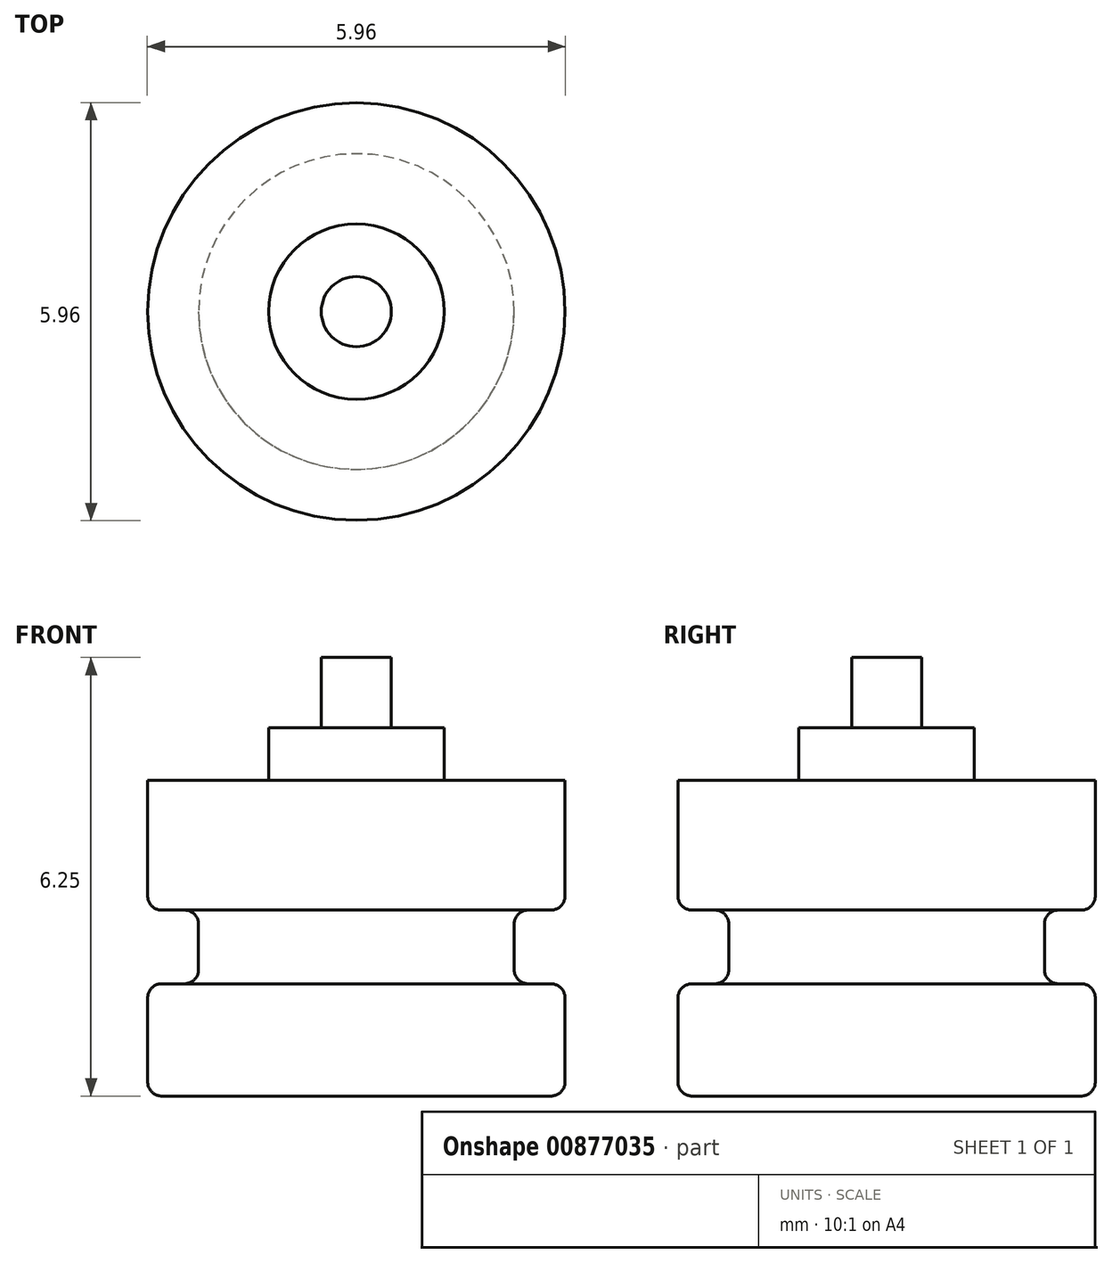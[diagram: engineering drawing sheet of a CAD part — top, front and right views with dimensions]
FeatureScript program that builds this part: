
annotation { "Feature Type Name" : "Feature", "Feature Type Description" : "" }
export const myFeature = defineFeature(function(context is Context, id is Id, definition is map)
    precondition{}
    {
        {
            var Q0;
            Q0=qCreatedBy(makeId("Front.planeOp"),FACE);
            var sketch = newSketch(context, id + "F0", { "sketchPlane" : qUnion([Q0])});
            skLineSegment(sketch, "E0", {"start": v(0, 0) * mm, "end": v(-2.97, 0) * mm});
            skLineSegment(sketch, "E1", {"start": v(-2.98, 0) * mm, "end": v(-2.98, 1.6) * mm});
            skLineSegment(sketch, "E2", {"start": v(-2.97, 1.6) * mm, "end": v(-2.25, 1.6) * mm});
            skLineSegment(sketch, "E3", {"start": v(-2.25, 1.6) * mm, "end": v(-2.25, 2.65) * mm});
            skLineSegment(sketch, "E4", {"start": v(-2.25, 2.65) * mm, "end": v(-2.98, 2.65) * mm});
            skLineSegment(sketch, "E5", {"start": v(-2.98, 2.65) * mm, "end": v(-2.98, 4.5) * mm});
            skLineSegment(sketch, "E6", {"start": v(-2.98, 4.5) * mm, "end": v(-1.25, 4.5) * mm});
            skLineSegment(sketch, "E7", {"start": v(-1.25, 4.5) * mm, "end": v(-1.25, 5.25) * mm});
            skLineSegment(sketch, "E8", {"start": v(-1.25, 5.25) * mm, "end": v(-0.5, 5.25) * mm});
            skLineSegment(sketch, "E9", {"start": v(-0.5, 5.25) * mm, "end": v(-0.5, 6.25) * mm});
            skLineSegment(sketch, "E10", {"start": v(-0.5, 6.25) * mm, "end": v(0, 6.25) * mm});
            skLineSegment(sketch, "E11", {"start": v(0, 6.25) * mm, "end": v(0, 0) * mm});
            skSolve(sketch);
        }
        {
            var Q0;
            Q0=makeQuery(id+"F0.imprint","IMPRINT",FACE,{"disambiguationData":[TD([[makeQuery(id+"F0.imprint","IMPRINT",EDGE,{"derivedFrom":sQuery(id+"F0.wireOp",EDGE,"E0")}),-1.0]])]});
            var Q1;
            Q1=sQuery(id+"F0.wireOp",EDGE,"E11");
            revolve(context, id + "F1", {"surfaceOperationType" : NewSurfaceOperationType.NEW, "entities" : qUnion([Q0]), "axis" : qUnion([Q1]), "revolveType" : RevolveType.FULL});
        }
        {
            var Q0;
            Q0=makeQuery(id+"F1.opRevolve","SWEPT_EDGE",EDGE,{"disambiguationData":[OSD([sQuery(id+"F0.wireOp",EDGE,"E4"),sQuery(id+"F0.wireOp",EDGE,"E5")])]});
            var Q1;
            Q1=makeQuery(id+"F1.opRevolve","SWEPT_EDGE",EDGE,{"disambiguationData":[OSD([sQuery(id+"F0.wireOp",EDGE,"E2"),sQuery(id+"F0.wireOp",EDGE,"E3")])]});
            var Q2;
            Q2=makeQuery(id+"F1.opRevolve","SWEPT_EDGE",EDGE,{"disambiguationData":[OSD([sQuery(id+"F0.wireOp",EDGE,"E3"),sQuery(id+"F0.wireOp",EDGE,"E4")])]});
            var Q3;
            Q3=makeQuery(id+"F1.opRevolve","SWEPT_EDGE",EDGE,{"disambiguationData":[OSD([sQuery(id+"F0.wireOp",EDGE,"E1"),sQuery(id+"F0.wireOp",EDGE,"E2")])]});
            var Q4;
            Q4=makeQuery(id+"F1.opRevolve","SWEPT_EDGE",EDGE,{"disambiguationData":[OSD([sQuery(id+"F0.wireOp",EDGE,"E0"),sQuery(id+"F0.wireOp",EDGE,"E1")])]});
            fillet(context, id + "F2", {"entities" : qUnion([Q0, Q1, Q2, Q3, Q4]), "radius" : .2 * mm, "tangentPropagation" : true, "allowEdgeOverflow" : false});
        }
    });
